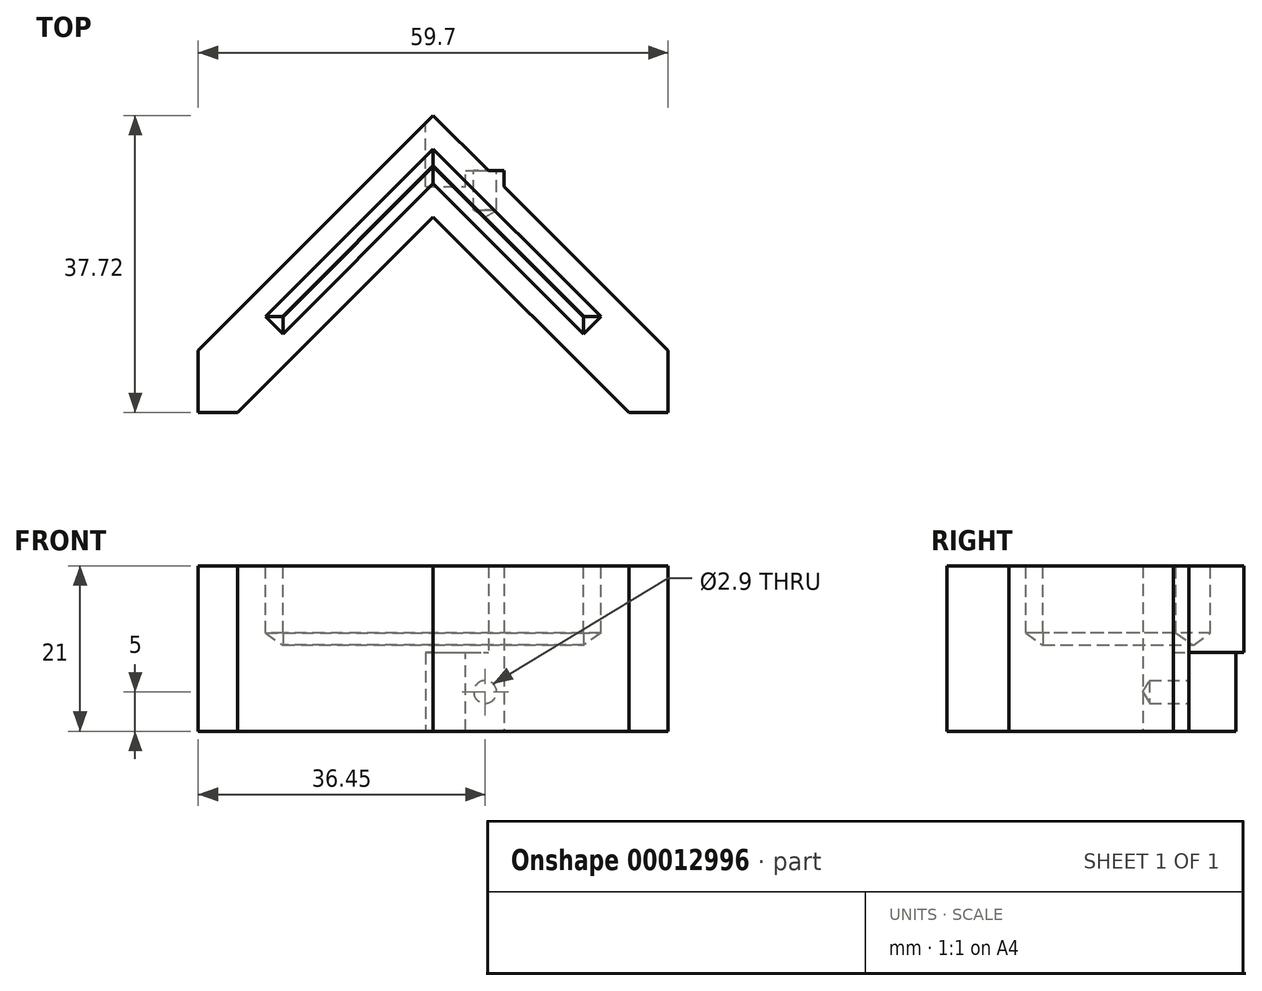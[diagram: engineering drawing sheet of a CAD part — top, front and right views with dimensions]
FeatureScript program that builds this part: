
annotation { "Feature Type Name" : "Feature", "Feature Type Description" : "" }
export const myFeature = defineFeature(function(context is Context, id is Id, definition is map)
    precondition{}
    {
        {
            var Q0;
            Q0=qCreatedBy(makeId("Top.planeOp"),FACE);
            var sketch = newSketch(context, id + "F0", { "sketchPlane" : qUnion([Q0])});
            skLineSegment(sketch, "E0", {"start": v(0, 29.1) * mm, "end": v(19.1, 10) * mm, "construction": true});
            skLineSegment(sketch, "E1", {"start": v(19.1, 10) * mm, "end": v(21.28, 12.2) * mm, "construction": true});
            skLineSegment(sketch, "E2", {"start": v(21.28, 12.2) * mm, "end": v(0, 33.48) * mm, "construction": true});
            skLineSegment(sketch, "E3", {"start": v(0, 37.72) * mm, "end": v(29.85, 7.87) * mm});
            skLineSegment(sketch, "E4", {"start": v(29.85, 7.87) * mm, "end": v(29.85, 0) * mm});
            skLineSegment(sketch, "E5", {"start": v(29.85, 0) * mm, "end": v(24.85, 0) * mm});
            skLineSegment(sketch, "E6", {"start": v(24.85, 0) * mm, "end": v(0, 24.85) * mm});
            skLineSegment(sketch, "E7.MirrorCS", {"start": v(0, 37.72) * mm, "end": v(-29.85, 7.87) * mm});
            skLineSegment(sketch, "E8.MirrorCS", {"start": v(-29.85, 7.87) * mm, "end": v(-29.85, 0) * mm});
            skLineSegment(sketch, "E9.MirrorCS", {"start": v(-24.85, 0) * mm, "end": v(0, 24.85) * mm});
            skLineSegment(sketch, "E10.MirrorCS", {"start": v(-29.85, 0) * mm, "end": v(-24.85, 0) * mm});
            skSolve(sketch);
        }
        {
            var Q0;
            Q0=makeQuery(id+"F0.imprint","IMPRINT",FACE,{"disambiguationData":[TD([[makeQuery(id+"F0.imprint","IMPRINT",EDGE,{"derivedFrom":sQuery(id+"F0.wireOp",EDGE,"E3")}),-1.0]])]});
            extrude(context, id + "F1", {"entities" : qUnion([Q0]), "depth" : 21 * mm});
        }
        {
            var Q0;
            Q0=makeQuery(id+"F1.opExtrude","CAP_FACE",FACE,{"disambiguationData":[OSD([sQuery(id+"F0.wireOp",EDGE,"E3"),sQuery(id+"F0.wireOp",EDGE,"E4"),sQuery(id+"F0.wireOp",EDGE,"E5"),sQuery(id+"F0.wireOp",EDGE,"E6"),sQuery(id+"F0.wireOp",EDGE,"E7.MirrorCS"),sQuery(id+"F0.wireOp",EDGE,"E8.MirrorCS"),sQuery(id+"F0.wireOp",EDGE,"E9.MirrorCS"),sQuery(id+"F0.wireOp",EDGE,"E10.MirrorCS")])],"isStart":false});
            var sketch = newSketch(context, id + "F2", { "sketchPlane" : qUnion([Q0])});
            skLineSegment(sketch, "E11", {"start": v(21.28, 12.2) * mm, "end": v(0, 33.48) * mm});
            skLineSegment(sketch, "E12", {"start": v(19.1, 10) * mm, "end": v(21.28, 12.2) * mm});
            skLineSegment(sketch, "E13", {"start": v(0, 29.1) * mm, "end": v(19.1, 10) * mm});
            skLineSegment(sketch, "E14.MirrorCS", {"start": v(0, 29.1) * mm, "end": v(-19.1, 10) * mm});
            skLineSegment(sketch, "E15.MirrorCS", {"start": v(-21.28, 12.2) * mm, "end": v(0, 33.48) * mm});
            skLineSegment(sketch, "E16.MirrorCS", {"start": v(-19.1, 10) * mm, "end": v(-21.28, 12.2) * mm});
            skSolve(sketch);
        }
        {
            var Q0;
            Q0=makeQuery(id+"F2.imprint","IMPRINT",FACE,{"disambiguationData":[TD([[makeQuery(id+"F2.imprint","IMPRINT",EDGE,{"derivedFrom":sQuery(id+"F2.wireOp",EDGE,"E11")}),1.0]])]});
            extrude(context, id + "F3", {"entities" : qUnion([Q0]), "operationType" : NewBodyOperationType.REMOVE, "oppositeDirection" : true, "depth" : 10 * mm});
        }
        {
            var Q0;
            Q0=makeQuery(id+"F1.opExtrude","CAP_FACE",FACE,{"disambiguationData":[OSD([sQuery(id+"F0.wireOp",EDGE,"E3"),sQuery(id+"F0.wireOp",EDGE,"E4"),sQuery(id+"F0.wireOp",EDGE,"E5"),sQuery(id+"F0.wireOp",EDGE,"E6"),sQuery(id+"F0.wireOp",EDGE,"E7.MirrorCS"),sQuery(id+"F0.wireOp",EDGE,"E8.MirrorCS"),sQuery(id+"F0.wireOp",EDGE,"E9.MirrorCS"),sQuery(id+"F0.wireOp",EDGE,"E10.MirrorCS")])],"isStart":true});
            var sketch = newSketch(context, id + "F4", { "sketchPlane" : qUnion([Q0])});
            skLineSegment(sketch, "E17", {"start": v(-1, -30.72) * mm, "end": v(-1, -36.72) * mm});
            skLineSegment(sketch, "E18", {"start": v(-1, -36.72) * mm, "end": v(0, -37.72) * mm});
            skLineSegment(sketch, "E19", {"start": v(0, -37.72) * mm, "end": v(11.22, -26.5) * mm});
            skLineSegment(sketch, "E20", {"start": v(4, -30.72) * mm, "end": v(4, -33.72) * mm, "construction": true});
            skLineSegment(sketch, "E21", {"start": v(-1, -30.72) * mm, "end": v(7, -30.72) * mm});
            skLineSegment(sketch, "E22", {"start": v(7, -30.72) * mm, "end": v(9, -30.72) * mm});
            skLineSegment(sketch, "E23", {"start": v(9, -30.72) * mm, "end": v(9, -28.72) * mm});
            skLineSegment(sketch, "E24", {"start": v(9, -28.72) * mm, "end": v(7, -30.72) * mm});
            skSolve(sketch);
        }
        {
            var Q0;
            Q0=makeQuery(id+"F4.imprint","IMPRINT",FACE,{"disambiguationData":[TD([[makeQuery(id+"F4.imprint","IMPRINT",EDGE,{"derivedFrom":sQuery(id+"F4.wireOp",EDGE,"9bdd0471-fe09-433f-a9cd-1460aa0bfd64")}),1.0]])]});
            var Q1;
            Q1=makeQuery(id+"F4.imprint","IMPRINT",FACE,{"disambiguationData":[TD([[makeQuery(id+"F4.imprint","IMPRINT",EDGE,{"derivedFrom":sQuery(id+"F4.wireOp",EDGE,"E17")}),1.0]])]});
            extrude(context, id + "F5", {"entities" : qUnion([Q0, Q1]), "operationType" : NewBodyOperationType.REMOVE, "oppositeDirection" : true, "depth" : 10 * mm});
        }
        {
            var Q0;
            Q0=makeQuery(id+"F4.imprint","IMPRINT",FACE,{"disambiguationData":[TD([[makeQuery(id+"F4.imprint","IMPRINT",EDGE,{"derivedFrom":sQuery(id+"F4.wireOp",EDGE,"E22")}),1.0]])]});
            extrude(context, id + "F6", {"entities" : qUnion([Q0]), "operationType" : NewBodyOperationType.ADD, "oppositeDirection" : true, "depth" : 21 * mm});
        }
        {
            var Q0;
            Q0=makeQuery(id+"F5.boolean.opBoolean","COPY",FACE,{"derivedFrom":makeQuery(id+"F5.opExtrude","SWEPT_FACE",FACE,{"disambiguationData":[OSD([sQuery(id+"F4.wireOp",EDGE,"E21")])]})});
            var sketch = newSketch(context, id + "F7", { "sketchPlane" : qUnion([Q0])});
            skPoint(sketch, "E25", {"position": v(-6.6, 5) * mm});
            skLineSegment(sketch, "E26.bottom", {"start": v(1, 0) * mm, "end": v(-4.1, 0) * mm});
            skLineSegment(sketch, "E26.top", {"start": v(1, 10) * mm, "end": v(-4.1, 10) * mm});
            skLineSegment(sketch, "E26.left", {"start": v(1, 0) * mm, "end": v(1, 10) * mm});
            skLineSegment(sketch, "E26.right", {"start": v(-4.1, 0) * mm, "end": v(-4.1, 10) * mm});
            skSolve(sketch);
        }
        {
            var Q0;
            Q0=makeQuery(id+"F7.imprint","IMPRINT",FACE,{"disambiguationData":[TD([[makeQuery(id+"F7.imprint","IMPRINT",EDGE,{"derivedFrom":sQuery(id+"F7.wireOp",EDGE,"E26.bottom")}),-1.0]])]});
            extrude(context, id + "F8", {"entities" : qUnion([Q0]), "operationType" : NewBodyOperationType.REMOVE, "oppositeDirection" : true, "depth" : 2 * mm});
        }
        {
            var Q0;
            Q0=makeQuery(id+"F6.boolean.opBoolean","MERGE",FACE,{"derivedFrom":[makeQuery(id+"F5.boolean.opBoolean","COPY",FACE,{"derivedFrom":makeQuery(id+"F5.opExtrude","SWEPT_FACE",FACE,{"disambiguationData":[OSD([sQuery(id+"F4.wireOp",EDGE,"E21")])]})}),makeQuery(id+"F6.opExtrude","SWEPT_FACE",FACE,{"disambiguationData":[OSD([sQuery(id+"F4.wireOp",EDGE,"E22")])]})]});
            var sketch = newSketch(context, id + "F9", { "sketchPlane" : qUnion([Q0])});
            skPoint(sketch, "E27", {"position": v(-6.6, 5) * mm});
            skSolve(sketch);
        }
        {
            var Q0;
            Q0=sQuery(id+"F9.wireOp",VERTEX,"E27");
            var Q1;
            Q1=makeQuery(id+"F1.opExtrude","SWEPT_BODY",BODY,{"disambiguationData":[OSD([sQuery(id+"F0.wireOp",EDGE,"E3"),sQuery(id+"F0.wireOp",EDGE,"E4"),sQuery(id+"F0.wireOp",EDGE,"E5"),sQuery(id+"F0.wireOp",EDGE,"E6"),sQuery(id+"F0.wireOp",EDGE,"E7.MirrorCS"),sQuery(id+"F0.wireOp",EDGE,"E8.MirrorCS"),sQuery(id+"F0.wireOp",EDGE,"E9.MirrorCS"),sQuery(id+"F0.wireOp",EDGE,"E10.MirrorCS")])]});
            hole(context, id + "F10", {"style" : HoleStyle.SIMPLE, "holeDiameter" : 2.9 * mm, "endStyle" : HoleEndStyle.BLIND, "holeDepth" : 5 * mm, "locations" : qUnion([Q0]), "scope" : qUnion([Q1])});
        }
        {
            var Q0;
            Q0=makeQuery(id+"F3.boolean.opBoolean","COPY",FACE,{"derivedFrom":makeQuery(id+"F3.opExtrude","CAP_FACE",FACE,{"disambiguationData":[OSD([sQuery(id+"F2.wireOp",EDGE,"E11"),sQuery(id+"F2.wireOp",EDGE,"E12"),sQuery(id+"F2.wireOp",EDGE,"E13"),sQuery(id+"F2.wireOp",EDGE,"E14.MirrorCS"),sQuery(id+"F2.wireOp",EDGE,"E15.MirrorCS"),sQuery(id+"F2.wireOp",EDGE,"E16.MirrorCS")])],"isStart":false})});
            chamfer(context, id + "F11", {"entities" : qUnion([Q0]), "width" : 1.5 * mm, "tangentPropagation" : true});
        }
    });
